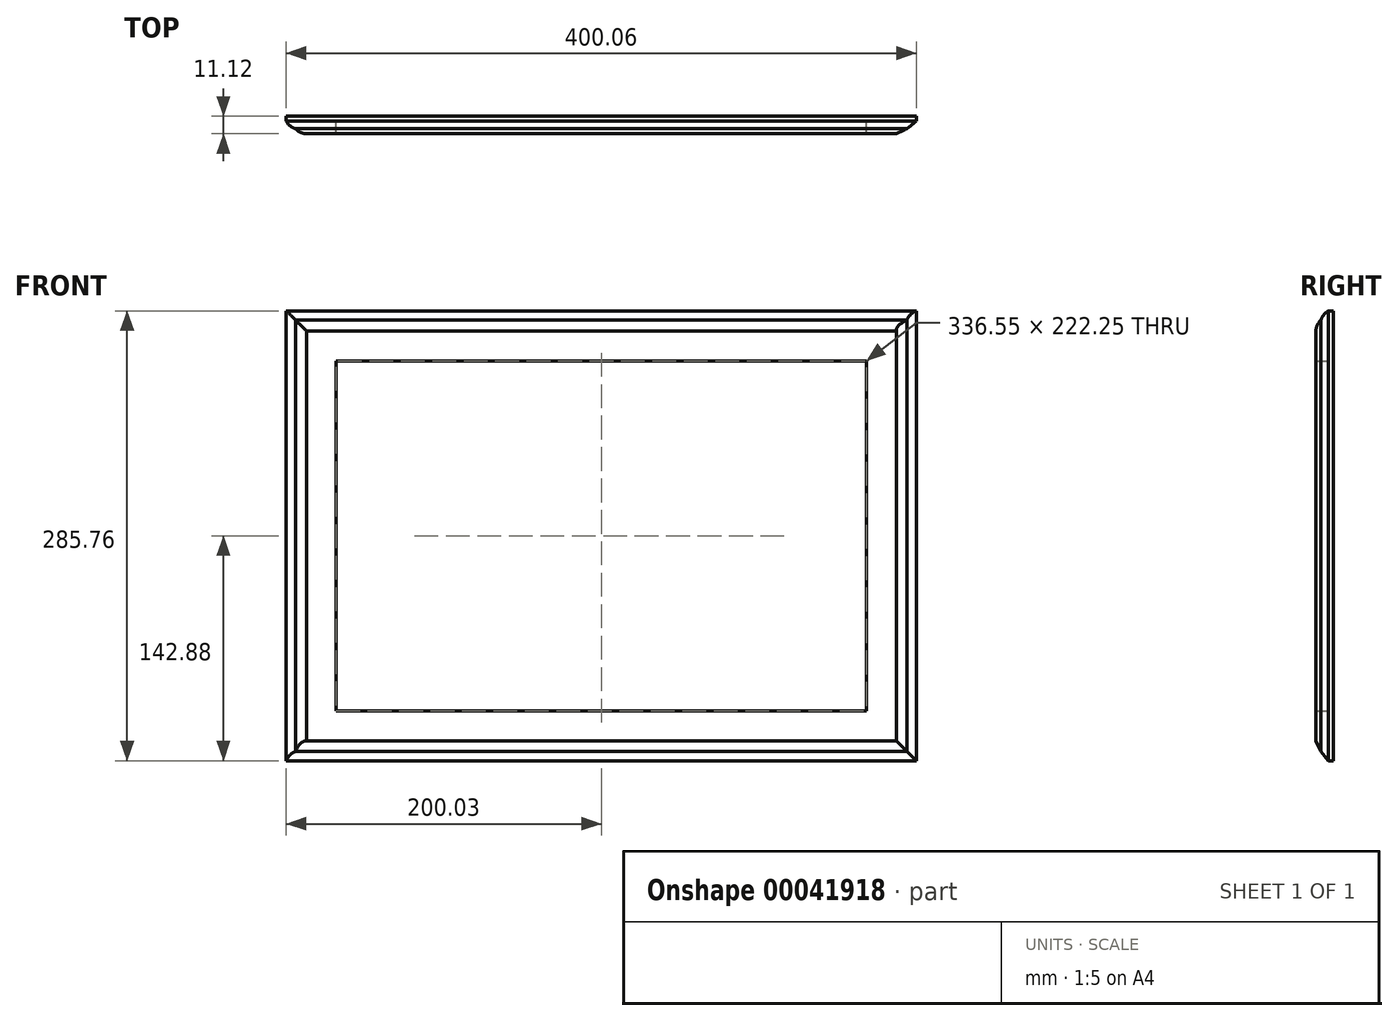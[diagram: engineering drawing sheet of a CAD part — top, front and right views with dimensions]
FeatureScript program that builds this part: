
annotation { "Feature Type Name" : "Feature", "Feature Type Description" : "" }
export const myFeature = defineFeature(function(context is Context, id is Id, definition is map)
    precondition{}
    {
        {
            var Q0;
            Q0=qCreatedBy(makeId("Front.planeOp"),FACE);
            var sketch = newSketch(context, id + "F0", { "sketchPlane" : qUnion([Q0])});
            skLineSegment(sketch, "E0.rect.bottom", {"start": v(168.28, 111.12) * mm, "end": v(-168.28, 111.12) * mm});
            skLineSegment(sketch, "E0.rect.top", {"start": v(168.28, -111.13) * mm, "end": v(-168.28, -111.13) * mm});
            skLineSegment(sketch, "E0.rect.left", {"start": v(168.28, 111.12) * mm, "end": v(168.28, -111.13) * mm});
            skLineSegment(sketch, "E0.rect.right", {"start": v(-168.28, 111.12) * mm, "end": v(-168.28, -111.13) * mm});
            skPoint(sketch, "E0.rect.middle", {"position": v(0, 0) * mm});
            skLineSegment(sketch, "E1.rect.bottom", {"start": v(-200.03, 142.87) * mm, "end": v(200.02, 142.88) * mm});
            skLineSegment(sketch, "E1.rect.top", {"start": v(-200.02, -142.88) * mm, "end": v(200.03, -142.88) * mm});
            skLineSegment(sketch, "E1.rect.left", {"start": v(-200.03, 142.87) * mm, "end": v(-200.02, -142.88) * mm});
            skLineSegment(sketch, "E1.rect.right", {"start": v(200.02, 142.88) * mm, "end": v(200.03, -142.87) * mm});
            skSolve(sketch);
        }
        {
            var Q0;
            Q0=makeQuery(id+"F0.imprint","IMPRINT",FACE,{"disambiguationData":[TD([[makeQuery(id+"F0.imprint","IMPRINT",EDGE,{"derivedFrom":sQuery(id+"F0.wireOp",EDGE,"E0.rect.bottom")}),-1.0]])]});
            extrude(context, id + "F1", {"entities" : qUnion([Q0]), "endBound" : BoundingType.SYMMETRIC, "depth" : 11.1 * mm});
        }
        {
            var Q0;
            Q0=qCreatedBy(makeId("Top.planeOp"),FACE);
            var sketch = newSketch(context, id + "F2", { "sketchPlane" : qUnion([Q0])});
            skArc(sketch, "E2", {"start": v(-194.16, -2.37) * mm, "mid": v(-191.07, -4.67) * mm, "end": v(-187.32, -5.56) * mm});
            skArc(sketch, "E3", {"start": v(-200.02, 2.38) * mm, "mid": v(-197.58, -0.6) * mm, "end": v(-194.16, -2.37) * mm});
            skLineSegment(sketch, "E4", {"start": v(-200.02, 2.38) * mm, "end": v(-194.16, -2.37) * mm, "construction": true});
            skLineSegment(sketch, "E5", {"start": v(-187.32, -5.56) * mm, "end": v(-194.16, -2.37) * mm, "construction": true});
            skLineSegment(sketch, "E6", {"start": v(-200.02, 2.38) * mm, "end": v(-200.02, -5.56) * mm});
            skLineSegment(sketch, "E7", {"start": v(-200.02, -5.56) * mm, "end": v(-187.32, -5.56) * mm});
            skLineSegment(sketch, "E8", {"start": v(0, 5.56) * mm, "end": v(0, -5.56) * mm, "construction": true});
            skLineSegment(sketch, "E9.MirrorCS", {"start": v(187.32, -5.56) * mm, "end": v(194.16, -2.37) * mm});
            skLineSegment(sketch, "E10.MirrorCS", {"start": v(200.02, 2.38) * mm, "end": v(194.16, -2.37) * mm});
            skArc(sketch, "E11.MirrorCS", {"start": v(200.02, 2.38) * mm, "mid": v(197.58, -0.6) * mm, "end": v(194.16, -2.37) * mm});
            skLineSegment(sketch, "E12.MirrorCS", {"start": v(200.02, 2.38) * mm, "end": v(200.02, -5.56) * mm});
            skArc(sketch, "E13.MirrorCS", {"start": v(194.16, -2.37) * mm, "mid": v(191.07, -4.67) * mm, "end": v(187.32, -5.56) * mm});
            skLineSegment(sketch, "E14.MirrorCS", {"start": v(200.02, -5.56) * mm, "end": v(187.32, -5.56) * mm});
            skSolve(sketch);
        }
        {
            var Q0;
            Q0 = qSketchRegion(id + "F2", true);
            extrude(context, id + "F3", {"entities" : qUnion([Q0]), "operationType" : NewBodyOperationType.REMOVE, "endBound" : BoundingType.THROUGH_ALL, "oppositeDirection" : true, "depth" : 25.4 * mm, "hasSecondDirection" : true, "secondDirectionBound" : SecondDirectionBoundingType.THROUGH_ALL, "secondDirectionOppositeDirection" : false, "secondDirectionDepth" : 25.4 * mm});
        }
        {
            var Q0;
            Q0=qCreatedBy(makeId("Right.planeOp"),FACE);
            var sketch = newSketch(context, id + "F4", { "sketchPlane" : qUnion([Q0])});
            skLineSegment(sketch, "E15", {"start": v(-5.56, 130.17) * mm, "end": v(-5.56, 142.87) * mm});
            skLineSegment(sketch, "E16", {"start": v(-5.56, 142.87) * mm, "end": v(2.38, 142.87) * mm});
            skArc(sketch, "E17", {"start": v(-2.37, 137.01) * mm, "mid": v(-4.67, 133.92) * mm, "end": v(-5.56, 130.17) * mm});
            skArc(sketch, "E18", {"start": v(2.38, 142.88) * mm, "mid": v(-0.6, 140.43) * mm, "end": v(-2.37, 137.01) * mm});
            skLineSegment(sketch, "E19", {"start": v(2.38, 142.87) * mm, "end": v(-2.37, 137.01) * mm, "construction": true});
            skLineSegment(sketch, "E20", {"start": v(-5.56, 130.17) * mm, "end": v(-2.37, 137.01) * mm, "construction": true});
            skLineSegment(sketch, "E21", {"start": v(5.56, 0) * mm, "end": v(-5.56, 0) * mm, "construction": true});
            skLineSegment(sketch, "E22.MirrorCS", {"start": v(-5.56, -130.17) * mm, "end": v(-5.56, -142.87) * mm});
            skLineSegment(sketch, "E23.MirrorCS", {"start": v(-5.56, -142.87) * mm, "end": v(2.38, -142.87) * mm});
            skArc(sketch, "E24.MirrorCS", {"start": v(2.38, -142.88) * mm, "mid": v(-0.6, -140.43) * mm, "end": v(-2.37, -137.01) * mm});
            skLineSegment(sketch, "E25.MirrorCS", {"start": v(2.38, -142.87) * mm, "end": v(-2.37, -137.01) * mm});
            skLineSegment(sketch, "E26.MirrorCS", {"start": v(-5.56, -130.17) * mm, "end": v(-2.37, -137.01) * mm});
            skArc(sketch, "E27.MirrorCS", {"start": v(-2.37, -137.01) * mm, "mid": v(-4.67, -133.92) * mm, "end": v(-5.56, -130.17) * mm});
            skSolve(sketch);
        }
        {
            var Q0;
            Q0 = qSketchRegion(id + "F4", true);
            extrude(context, id + "F5", {"entities" : qUnion([Q0]), "operationType" : NewBodyOperationType.REMOVE, "endBound" : BoundingType.THROUGH_ALL, "oppositeDirection" : true, "depth" : 25.4 * mm, "hasSecondDirection" : true, "secondDirectionBound" : SecondDirectionBoundingType.THROUGH_ALL, "secondDirectionOppositeDirection" : false, "secondDirectionDepth" : 25.4 * mm});
        }
    });
